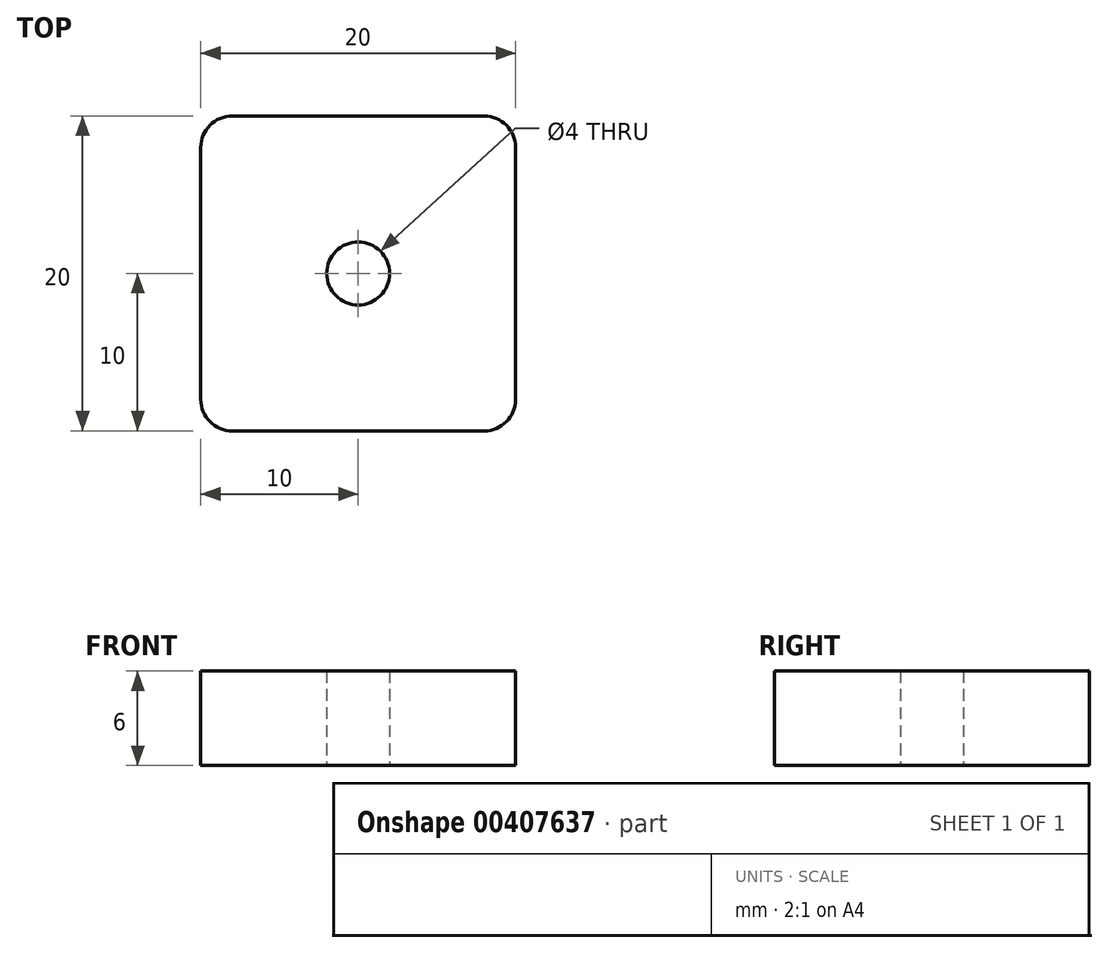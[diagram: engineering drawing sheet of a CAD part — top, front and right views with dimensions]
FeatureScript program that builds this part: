
annotation { "Feature Type Name" : "Feature", "Feature Type Description" : "" }
export const myFeature = defineFeature(function(context is Context, id is Id, definition is map)
    precondition{}
    {
        {
            var Q0;
            Q0=qCreatedBy(makeId("Top.planeOp"),FACE);
            var sketch = newSketch(context, id + "F0", { "sketchPlane" : qUnion([Q0])});
            skLineSegment(sketch, "E0.bottom", {"start": v(8, 10) * mm, "end": v(-8, 10) * mm});
            skLineSegment(sketch, "E0.top", {"start": v(8, -10) * mm, "end": v(-8, -10) * mm});
            skLineSegment(sketch, "E0.left", {"start": v(10, 8) * mm, "end": v(10, -8) * mm});
            skLineSegment(sketch, "E0.right", {"start": v(-10, 8) * mm, "end": v(-10, -8) * mm});
            skPoint(sketch, "E0.middle", {"position": v(0, 0) * mm});
            skCircle(sketch, "E1", {"center": v(0, 0) * mm, "radius": 2 * mm});
            skPoint(sketch, "E2.visualSharp", {"position": v(-10, 10) * mm});
            skArc(sketch, "E2.filletArc", {"start": v(-8, 10) * mm, "mid": v(-9.41, 9.41) * mm, "end": v(-10, 8) * mm});
            skPoint(sketch, "E3.visualSharp", {"position": v(-10, -10) * mm});
            skArc(sketch, "E3.filletArc", {"start": v(-10, -8) * mm, "mid": v(-9.41, -9.41) * mm, "end": v(-8, -10) * mm});
            skPoint(sketch, "E4.visualSharp", {"position": v(10, -10) * mm});
            skArc(sketch, "E4.filletArc", {"start": v(8, -10) * mm, "mid": v(9.41, -9.41) * mm, "end": v(10, -8) * mm});
            skPoint(sketch, "E5.visualSharp", {"position": v(10, 10) * mm});
            skArc(sketch, "E5.filletArc", {"start": v(10, 8) * mm, "mid": v(9.41, 9.41) * mm, "end": v(8, 10) * mm});
            skSolve(sketch);
        }
        {
            var Q0;
            Q0=makeQuery(id+"F0.imprint","IMPRINT",FACE,{"disambiguationData":[TD([[makeQuery(id+"F0.imprint","IMPRINT",EDGE,{"derivedFrom":sQuery(id+"F0.wireOp",EDGE,"E0.bottom")}),1.0]])]});
            extrude(context, id + "F1", {"entities" : qUnion([Q0]), "depth" : 6 * mm});
        }
    });
